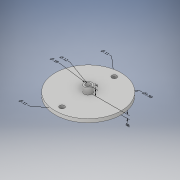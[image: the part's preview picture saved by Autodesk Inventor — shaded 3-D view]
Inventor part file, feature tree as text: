
AUTODESK INVENTOR PART (.ipt)
format: ipt  version: 2018 (Build 220112000, 112)  size: 145,408 bytes
history: native  units: in
note: dims shown in document units (in); Inventor stores cm internally (conversion verified against a paired STEP export)
features: other x8, sketch x6, extrude x4, hole x2
ambient origin geometry x8: Origin, YZ Plane, XZ Plane, XY Plane, X Axis, Y Axis, Z Axis, Center Point
bodies: Solid1 (feature_tree)
feature tree (20):
  other  "Annotations"
  extrude  "Extrusion1"  Depth=0.08in TaperAngle=0.0deg
  extrude  "Extrusion3"  Depth=0.14in TaperAngle=0.0deg
  extrude  "Extrusion4"  Depth=0.18in TaperAngle=0.0deg
  extrude  "Extrusion5"  Depth=0.18in TaperAngle=0.0deg
  hole  "Hole2"  [1 undecoded]
  hole  "Hole3"  [1 undecoded]
  sketch  "Sketch1"  dims[d0=1.5in d1=0.08in d2=0.0in]
  sketch  "Sketch5"  dims[d14=0.18in d15=0.14in d16=0.0in]
  sketch  "Sketch6"  dims[d17=0.115in d18=0.18in d19=0.0in]
  sketch  "Sketch7"  dims[d20=0.08in d21=0.18in d22=0.0in]
  sketch  "Sketch8"  dims[d23=0.155in d24=0.155in]
  sketch  "Sketch9"  dims[d25=0.11in d26=0.75in d27=0.375in d28=0.25in d29=0.5635in d30=0.2in d31=0.8108in d32=0.155in d33=0.11in d34=0.75in d35=0.375in d36=0.25in d37=0.5635in d38=0.2in d39=0.8108in d40=0.9476in d41=0.1849in d42=0.3681in d43=0.11in d44=1.5322in d45=0.1836in d46=0.3709in d47=0.11in d48=2.335in d49=0.115in d50=2.4217in d51=0.18in d52=0.14in d53=0.08in d54=1.7237in d55=0.3937in d56=0.2269in d57=1.5in]
  other  "Diameter Dimension 1"
  other  "Diameter Dimension 2"
  other  "Diameter Dimension 3"
  other  "Diameter Dimension 4"
  other  "Linear Dimension 1"
  other  "Linear Dimension 2"
  other  "Diameter Dimension 5"
note: 2 required parameter values undecoded (feature->parameter linkage not recoverable at this tier; creation-order binding heuristic only, values carry confidence <= 0.55)
